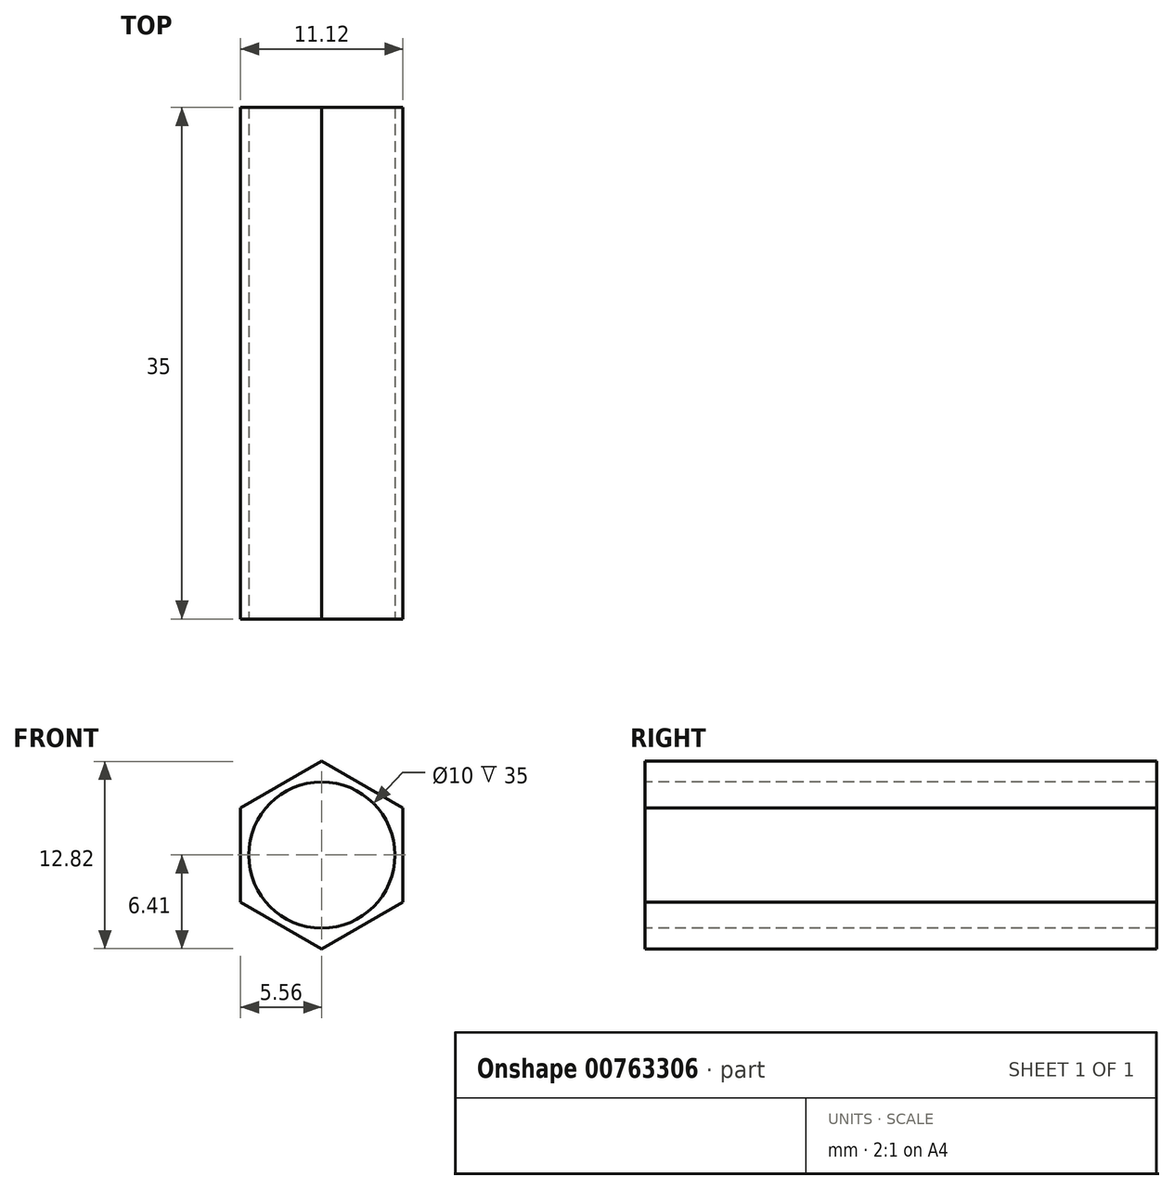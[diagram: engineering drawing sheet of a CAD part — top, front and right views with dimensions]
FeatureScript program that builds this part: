
annotation { "Feature Type Name" : "Feature", "Feature Type Description" : "" }
export const myFeature = defineFeature(function(context is Context, id is Id, definition is map)
    precondition{}
    {
        {
            var Q0;
            Q0=qCreatedBy(makeId("Front.planeOp"),FACE);
            var sketch = newSketch(context, id + "F0", { "sketchPlane" : qUnion([Q0])});
            skCircle(sketch, "E0.cCircle", {"center": v(0, 0) * mm, "radius": 5.55 * mm, "construction": true});
            skLineSegment(sketch, "E0.0", {"start": v(5.55, 3.2) * mm, "end": v(5.55, -3.2) * mm});
            skLineSegment(sketch, "E0.1", {"start": v(5.56, -3.2) * mm, "end": v(0, -6.41) * mm});
            skLineSegment(sketch, "E0.2", {"start": v(0, -6.41) * mm, "end": v(-5.55, -3.2) * mm});
            skLineSegment(sketch, "E0.3", {"start": v(-5.55, -3.2) * mm, "end": v(-5.56, 3.2) * mm});
            skLineSegment(sketch, "E0.4", {"start": v(-5.56, 3.2) * mm, "end": v(0, 6.41) * mm});
            skLineSegment(sketch, "E0.5", {"start": v(0, 6.41) * mm, "end": v(5.56, 3.2) * mm});
            skPoint(sketch, "E0.0.midPoint", {"position": v(5.55, 0) * mm});
            skSolve(sketch);
        }
        {
            var Q0;
            Q0=makeQuery(id+"F0.imprint","IMPRINT",FACE,{"disambiguationData":[TD([[makeQuery(id+"F0.imprint","IMPRINT",EDGE,{"derivedFrom":sQuery(id+"F0.wireOp",EDGE,"E0.0")}),-1.0]])]});
            extrude(context, id + "F1", {"entities" : qUnion([Q0]), "depth" : 35 * mm, "offsetDistance" : 25 * mm});
        }
        {
            var Q0;
            Q0=makeQuery(id+"F1.opExtrude","CAP_FACE",FACE,{"disambiguationData":[OSD([sQuery(id+"F0.wireOp",EDGE,"E0.0"),sQuery(id+"F0.wireOp",EDGE,"E0.1"),sQuery(id+"F0.wireOp",EDGE,"E0.2"),sQuery(id+"F0.wireOp",EDGE,"E0.3"),sQuery(id+"F0.wireOp",EDGE,"E0.4"),sQuery(id+"F0.wireOp",EDGE,"E0.5")])],"isStart":false});
            var sketch = newSketch(context, id + "F2", { "sketchPlane" : qUnion([Q0])});
            skCircle(sketch, "E1", {"center": v(0, 0) * mm, "radius": 5 * mm});
            skSolve(sketch);
        }
        {
            var Q0;
            Q0=makeQuery(id+"F2.imprint","IMPRINT",FACE,{"disambiguationData":[TD([[makeQuery(id+"F2.imprint","IMPRINT",EDGE,{"derivedFrom":sQuery(id+"F2.wireOp",EDGE,"E1")}),1.0]])]});
            extrude(context, id + "F3", {"entities" : qUnion([Q0]), "operationType" : NewBodyOperationType.REMOVE, "oppositeDirection" : true, "depth" : 63.8 * mm, "offsetDistance" : 25 * mm});
        }
    });
